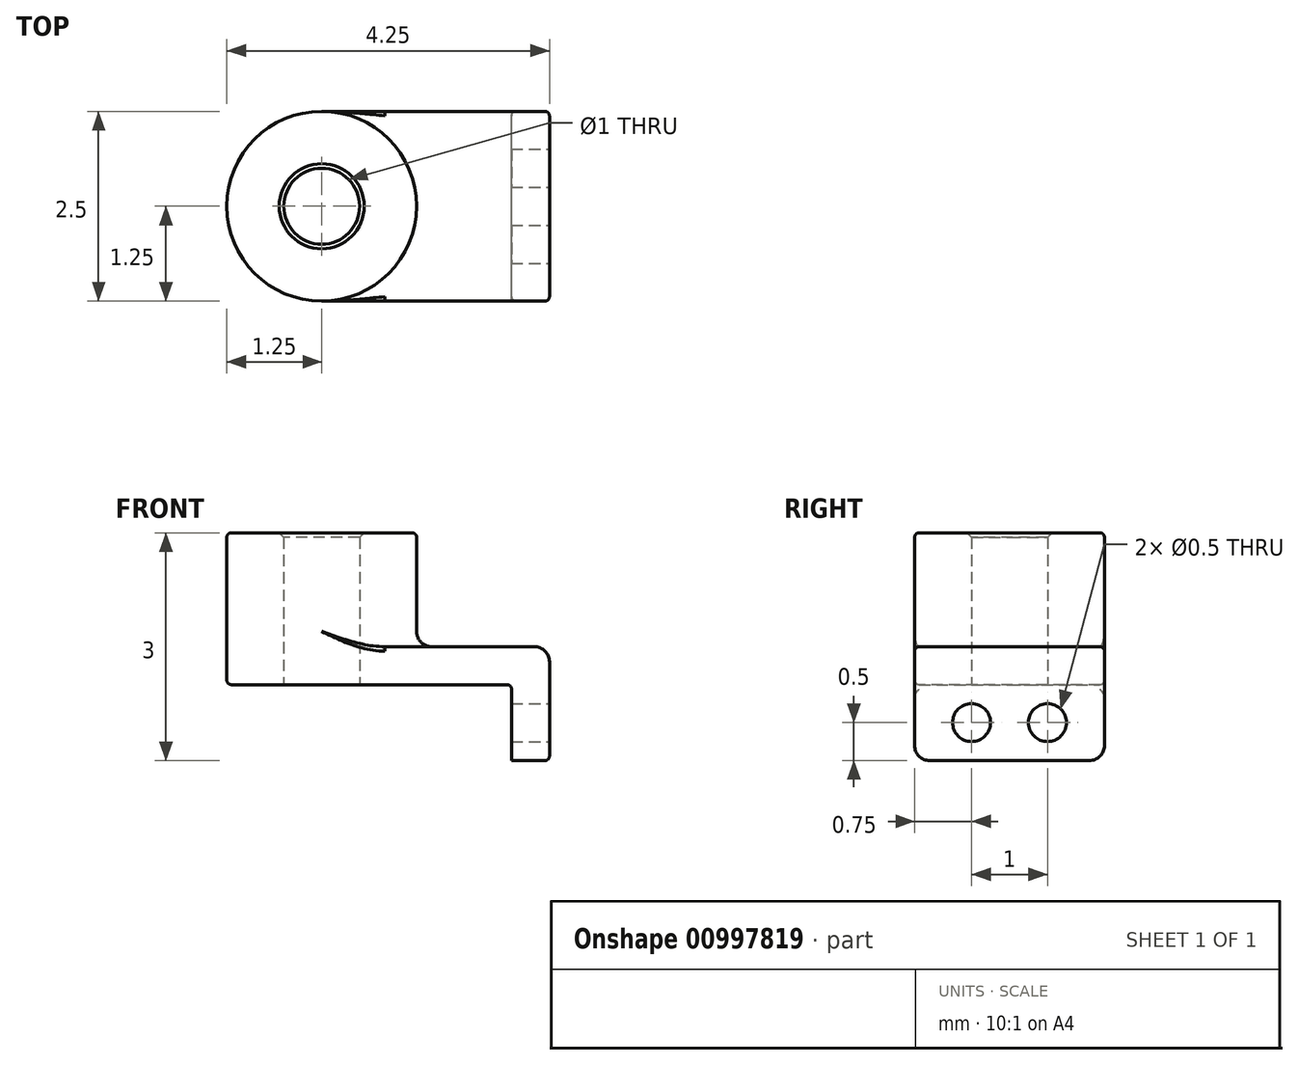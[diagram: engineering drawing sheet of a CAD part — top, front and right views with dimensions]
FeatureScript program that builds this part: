
annotation { "Feature Type Name" : "Feature", "Feature Type Description" : "" }
export const myFeature = defineFeature(function(context is Context, id is Id, definition is map)
    precondition{}
    {
        {
            var Q0;
            Q0=qCreatedBy(makeId("Top.planeOp"),FACE);
            var sketch = newSketch(context, id + "F0", { "sketchPlane" : qUnion([Q0])});
            skLineSegment(sketch, "E0.bottom", {"start": v(1.5, 1.25) * mm, "end": v(-1.5, 1.25) * mm});
            skLineSegment(sketch, "E0.top", {"start": v(1.5, -1.25) * mm, "end": v(-1.5, -1.25) * mm});
            skLineSegment(sketch, "E0.left", {"start": v(1.5, 1.25) * mm, "end": v(1.5, -1.25) * mm});
            skLineSegment(sketch, "E0.right", {"start": v(-1.5, 1.25) * mm, "end": v(-1.5, -1.25) * mm});
            skPoint(sketch, "E0.middle", {"position": v(0, 0) * mm});
            skCircle(sketch, "E1", {"center": v(-1.5, 0) * mm, "radius": 1.25 * mm});
            skCircle(sketch, "E2", {"center": v(-1.5, 0) * mm, "radius": 0.5 * mm});
            skSolve(sketch);
        }
        {
            var Q0;
            {var subQ0=sQuery(id+"F0.wireOp",EDGE,"E0.bottom");Q0=makeQuery(id+"F0.imprint","IMPRINT",FACE,{"disambiguationData":[TD([[makeQuery(id+"F0.imprint","IMPRINT",EDGE,{"derivedFrom":subQ0}),1.0]])]});}
            var Q1;
            {var subQ1=sQuery(id+"F0.wireOp",EDGE,"E0.right");var subQ3=sQuery(id+"F0.wireOp",EDGE,"E2");var subQ4=makeQuery(id+"F0.imprint","INTERSECT",VERTEX,{"disambiguationData":[OD(0.0)],"derivedFrom":[subQ1,subQ3]});Q1=makeQuery(id+"F0.imprint","IMPRINT",FACE,{"disambiguationData":[TD([[makeQuery(id+"F0.imprint","IMPRINT",EDGE,{"disambiguationData":[TD([[subQ4,1.0]])],"derivedFrom":subQ3}),-1.0]])]});}
            var Q2;
            {var subQ1=sQuery(id+"F0.wireOp",EDGE,"E0.right");var subQ3=sQuery(id+"F0.wireOp",EDGE,"E2");var subQ4=makeQuery(id+"F0.imprint","INTERSECT",VERTEX,{"disambiguationData":[OD(0.0)],"derivedFrom":[subQ1,subQ3]});Q2=makeQuery(id+"F0.imprint","IMPRINT",FACE,{"disambiguationData":[TD([[makeQuery(id+"F0.imprint","IMPRINT",EDGE,{"disambiguationData":[TD([[subQ4,-1.0]])],"derivedFrom":subQ3}),-1.0]])]});}
            extrude(context, id + "F1", {"entities" : qUnion([Q0, Q1, Q2]), "depth" : 0.5 * mm, "offsetDistance" : 25 * mm});
        }
        {
            var Q0;
            {var subQ1=sQuery(id+"F0.wireOp",EDGE,"E0.right");var subQ3=sQuery(id+"F0.wireOp",EDGE,"E2");var subQ4=makeQuery(id+"F0.imprint","INTERSECT",VERTEX,{"disambiguationData":[OD(0.0)],"derivedFrom":[subQ1,subQ3]});Q0=makeQuery(id+"F0.imprint","IMPRINT",FACE,{"disambiguationData":[TD([[makeQuery(id+"F0.imprint","IMPRINT",EDGE,{"disambiguationData":[TD([[subQ4,1.0]])],"derivedFrom":subQ3}),-1.0]])]});}
            var Q1;
            {var subQ1=sQuery(id+"F0.wireOp",EDGE,"E0.right");var subQ3=sQuery(id+"F0.wireOp",EDGE,"E2");var subQ4=makeQuery(id+"F0.imprint","INTERSECT",VERTEX,{"disambiguationData":[OD(0.0)],"derivedFrom":[subQ1,subQ3]});Q1=makeQuery(id+"F0.imprint","IMPRINT",FACE,{"disambiguationData":[TD([[makeQuery(id+"F0.imprint","IMPRINT",EDGE,{"disambiguationData":[TD([[subQ4,-1.0]])],"derivedFrom":subQ3}),-1.0]])]});}
            extrude(context, id + "F2", {"entities" : qUnion([Q0, Q1]), "operationType" : NewBodyOperationType.ADD, "depth" : 2 * mm, "offsetDistance" : 25 * mm});
        }
        {
            var Q0;
            Q0=makeQuery(id+"F1.opExtrude","SWEPT_FACE",FACE,{"disambiguationData":[OSD([sQuery(id+"F0.wireOp",EDGE,"E0.left")])]});
            var sketch = newSketch(context, id + "F3", { "sketchPlane" : qUnion([Q0])});
            skLineSegment(sketch, "E3.bottom", {"start": v(-1.25, 0.5) * mm, "end": v(1.25, 0.5) * mm});
            skLineSegment(sketch, "E3.top", {"start": v(-1.25, -1) * mm, "end": v(1.25, -1) * mm});
            skLineSegment(sketch, "E3.left", {"start": v(-1.25, 0.5) * mm, "end": v(-1.25, -1) * mm});
            skLineSegment(sketch, "E3.right", {"start": v(1.25, 0.5) * mm, "end": v(1.25, -1) * mm});
            skCircle(sketch, "E4", {"center": v(-0.5, -0.5) * mm, "radius": 0.25 * mm});
            skLineSegment(sketch, "E5", {"start": v(0, 0.5) * mm, "end": v(0, -1) * mm, "construction": true});
            skCircle(sketch, "E6.MirrorC", {"center": v(0.5, -0.5) * mm, "radius": 0.25 * mm});
            skSolve(sketch);
        }
        {
            var Q0;
            Q0 = qSketchRegion(id + "F3", true);
            extrude(context, id + "F4", {"entities" : qUnion([Q0]), "operationType" : NewBodyOperationType.ADD, "oppositeDirection" : true, "depth" : 0.5 * mm, "offsetDistance" : 25 * mm});
        }
        {
            var Q0;
            {var subQ0=sQuery(id+"F0.wireOp",EDGE,"E1");Q0=makeQuery(id+"F2.boolean.opBoolean","INTERSECT",EDGE,{"derivedFrom":[makeQuery(id+"F1.opExtrude","CAP_FACE",FACE,{"disambiguationData":[OSD([sQuery(id+"F0.wireOp",EDGE,"E0.bottom"),sQuery(id+"F0.wireOp",EDGE,"E0.top"),sQuery(id+"F0.wireOp",EDGE,"E0.left"),subQ0,sQuery(id+"F0.wireOp",EDGE,"E2")])],"isStart":false}),makeQuery(id+"F2.opExtrude","SWEPT_FACE",FACE,{"disambiguationData":[OSD([subQ0])]})]});}
            var Q1;
            Q1=makeQuery(id+"F1.opExtrude","CAP_EDGE",EDGE,{"disambiguationData":[OSD([sQuery(id+"F0.wireOp",EDGE,"E0.left")])],"isStart":false});
            var Q2;
            Q2=makeQuery(id+"F4.opExtrude","SWEPT_EDGE",EDGE,{"disambiguationData":[OSD([sQuery(id+"F3.wireOp",EDGE,"E3.top"),sQuery(id+"F3.wireOp",EDGE,"E3.left")])]});
            var Q3;
            Q3=makeQuery(id+"F4.opExtrude","SWEPT_EDGE",EDGE,{"disambiguationData":[OSD([sQuery(id+"F3.wireOp",EDGE,"E3.top"),sQuery(id+"F3.wireOp",EDGE,"E3.right")])]});
            fillet(context, id + "F5", {"entities" : qUnion([Q0, Q1, Q2, Q3]), "radius" : 0.2 * mm, "tangentPropagation" : true, "allowEdgeOverflow" : false});
        }
        {
            var Q0;
            Q0=makeQuery(id+"F1.opExtrude","CAP_EDGE",EDGE,{"disambiguationData":[OSD([sQuery(id+"F0.wireOp",EDGE,"E0.top")])],"isStart":false});
            var Q1;
            Q1=makeQuery(id+"F1.opExtrude","CAP_EDGE",EDGE,{"disambiguationData":[OSD([sQuery(id+"F0.wireOp",EDGE,"E0.top")])],"isStart":true});
            var Q2;
            Q2=makeQuery(id+"F4.boolean.opBoolean","INTERSECT",EDGE,{"derivedFrom":[makeQuery(id+"F1.opExtrude","CAP_FACE",FACE,{"disambiguationData":[OSD([sQuery(id+"F0.wireOp",EDGE,"E0.bottom"),sQuery(id+"F0.wireOp",EDGE,"E0.top"),sQuery(id+"F0.wireOp",EDGE,"E0.left"),sQuery(id+"F0.wireOp",EDGE,"E1"),sQuery(id+"F0.wireOp",EDGE,"E2")])],"isStart":true}),makeQuery(id+"F4.opExtrude","CAP_FACE",FACE,{"disambiguationData":[OSD([sQuery(id+"F3.wireOp",EDGE,"E3.bottom"),sQuery(id+"F3.wireOp",EDGE,"E3.top"),sQuery(id+"F3.wireOp",EDGE,"E3.left"),sQuery(id+"F3.wireOp",EDGE,"E3.right"),sQuery(id+"F3.wireOp",EDGE,"E4"),sQuery(id+"F3.wireOp",EDGE,"E6.MirrorC")])],"isStart":false})]});
            var Q3;
            Q3=makeQuery(id+"F2.opExtrude","CAP_EDGE",EDGE,{"disambiguationData":[OSD([sQuery(id+"F0.wireOp",EDGE,"E1")])],"isStart":false});
            fillet(context, id + "F6", {"entities" : qUnion([Q0, Q1, Q2, Q3]), "radius" : 0.06 * mm, "tangentPropagation" : true, "allowEdgeOverflow" : false});
        }
        {
            var Q0;
            Q0=makeQuery(id+"F2.opExtrude","CAP_EDGE",EDGE,{"disambiguationData":[OSD([sQuery(id+"F0.wireOp",EDGE,"E2")])],"isStart":false});
            chamfer(context, id + "F7", {"entities" : qUnion([Q0]), "width" : 0.06 * mm, "tangentPropagation" : true});
        }
    });
